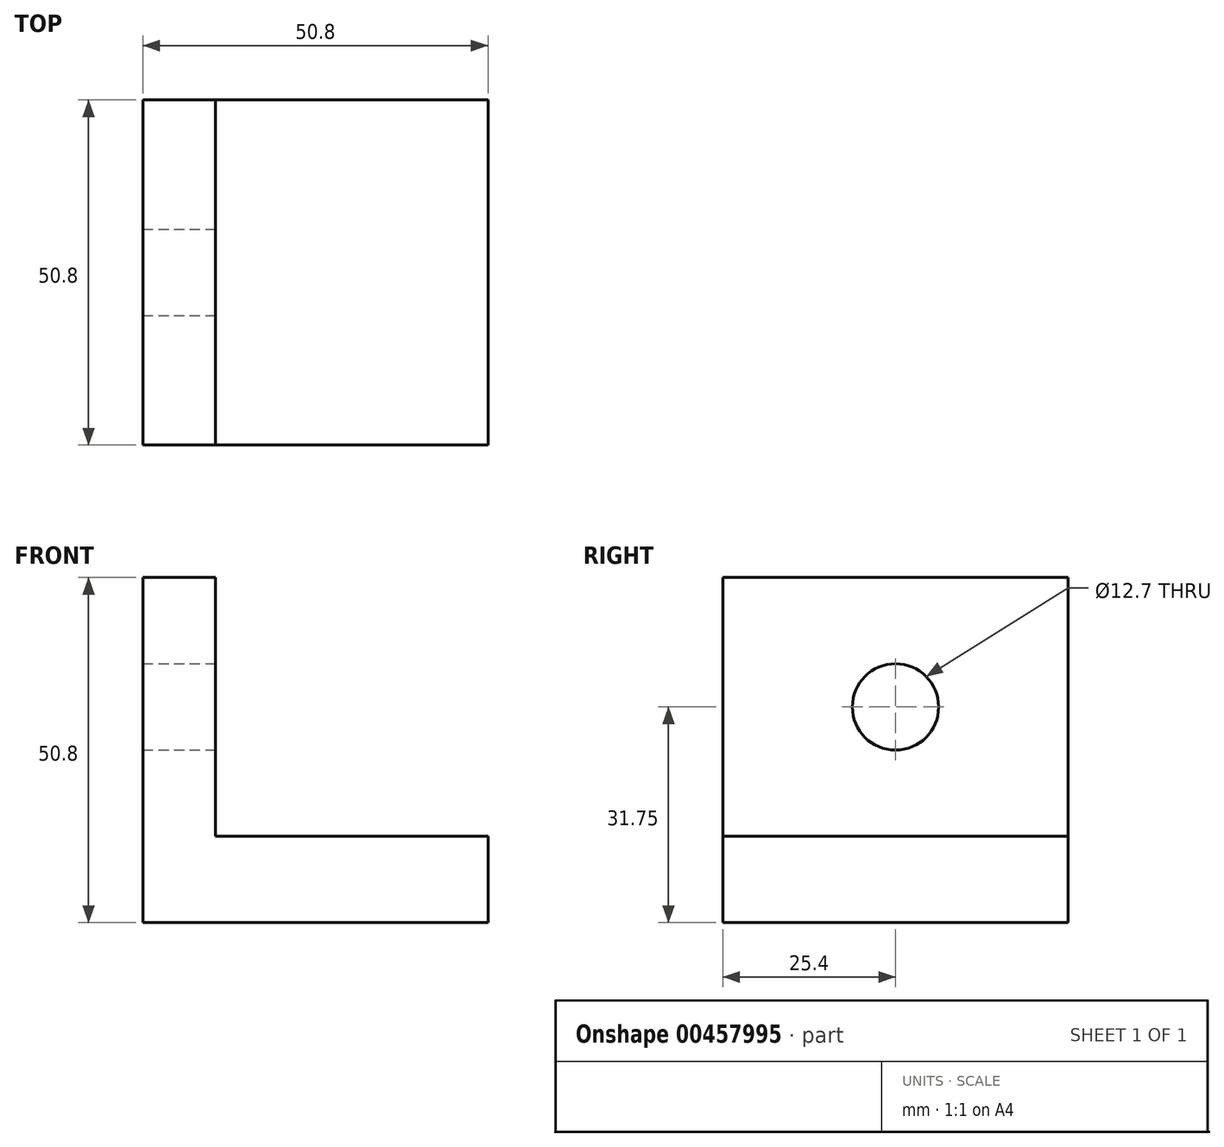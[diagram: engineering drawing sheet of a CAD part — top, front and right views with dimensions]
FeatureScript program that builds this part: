
annotation { "Feature Type Name" : "Feature", "Feature Type Description" : "" }
export const myFeature = defineFeature(function(context is Context, id is Id, definition is map)
    precondition{}
    {
        {
            var Q0;
            Q0=qCreatedBy(makeId("Front.planeOp"),FACE);
            var sketch = newSketch(context, id + "F0", { "sketchPlane" : qUnion([Q0])});
            skLineSegment(sketch, "E0", {"start": v(-73.99, 50.8) * mm, "end": v(-73.99, 0) * mm});
            skLineSegment(sketch, "E1", {"start": v(-73.99, 0) * mm, "end": v(-23.19, 0) * mm});
            skLineSegment(sketch, "E2", {"start": v(-23.19, 0) * mm, "end": v(-23.19, 12.7) * mm});
            skLineSegment(sketch, "E3", {"start": v(-23.19, 12.7) * mm, "end": v(-63.3, 12.7) * mm});
            skLineSegment(sketch, "E4", {"start": v(-63.3, 12.7) * mm, "end": v(-63.3, 50.8) * mm});
            skLineSegment(sketch, "E5", {"start": v(-63.3, 50.8) * mm, "end": v(-73.99, 50.8) * mm});
            skSolve(sketch);
        }
        {
            var Q0;
            Q0=makeQuery(id+"F0.imprint","IMPRINT",FACE,{"disambiguationData":[TD([[makeQuery(id+"F0.imprint","IMPRINT",EDGE,{"derivedFrom":sQuery(id+"F0.wireOp",EDGE,"E0")}),1.0]])]});
            extrude(context, id + "F1", {"entities" : qUnion([Q0]), "depth" : 50.8 * mm});
        }
        {
            var Q0;
            Q0=makeQuery(id+"F1.opExtrude","SWEPT_FACE",FACE,{"disambiguationData":[OSD([sQuery(id+"F0.wireOp",EDGE,"E4")])]});
            var sketch = newSketch(context, id + "F2", { "sketchPlane" : qUnion([Q0])});
            skCircle(sketch, "E6", {"center": v(-25.4, 31.75) * mm, "radius": 6.35 * mm});
            skPoint(sketch, "E6.centerSnap0", {"position": v(0, 31.75) * mm});
            skPoint(sketch, "E6.centerSnap1", {"position": v(-25.4, 12.7) * mm});
            skSolve(sketch);
        }
        {
            var Q0;
            Q0=sQuery(id+"F2.wireOp",VERTEX,"E6.center");
            var Q1;
            Q1=makeQuery(id+"F1.opExtrude","SWEPT_BODY",BODY,{"disambiguationData":[OSD([sQuery(id+"F0.wireOp",EDGE,"E0"),sQuery(id+"F0.wireOp",EDGE,"E1"),sQuery(id+"F0.wireOp",EDGE,"E2"),sQuery(id+"F0.wireOp",EDGE,"E3"),sQuery(id+"F0.wireOp",EDGE,"E4"),sQuery(id+"F0.wireOp",EDGE,"E5")])]});
            hole(context, id + "F3", {"style" : HoleStyle.SIMPLE, "endStyle" : HoleEndStyle.THROUGH, "holeDiameter" : 12.7 * mm, "isTappedThrough" : true, "tappedDepth" : 12.7 * mm, "tapClearance" : 3, "locations" : qUnion([Q0]), "scope" : qUnion([Q1])});
        }
    });
